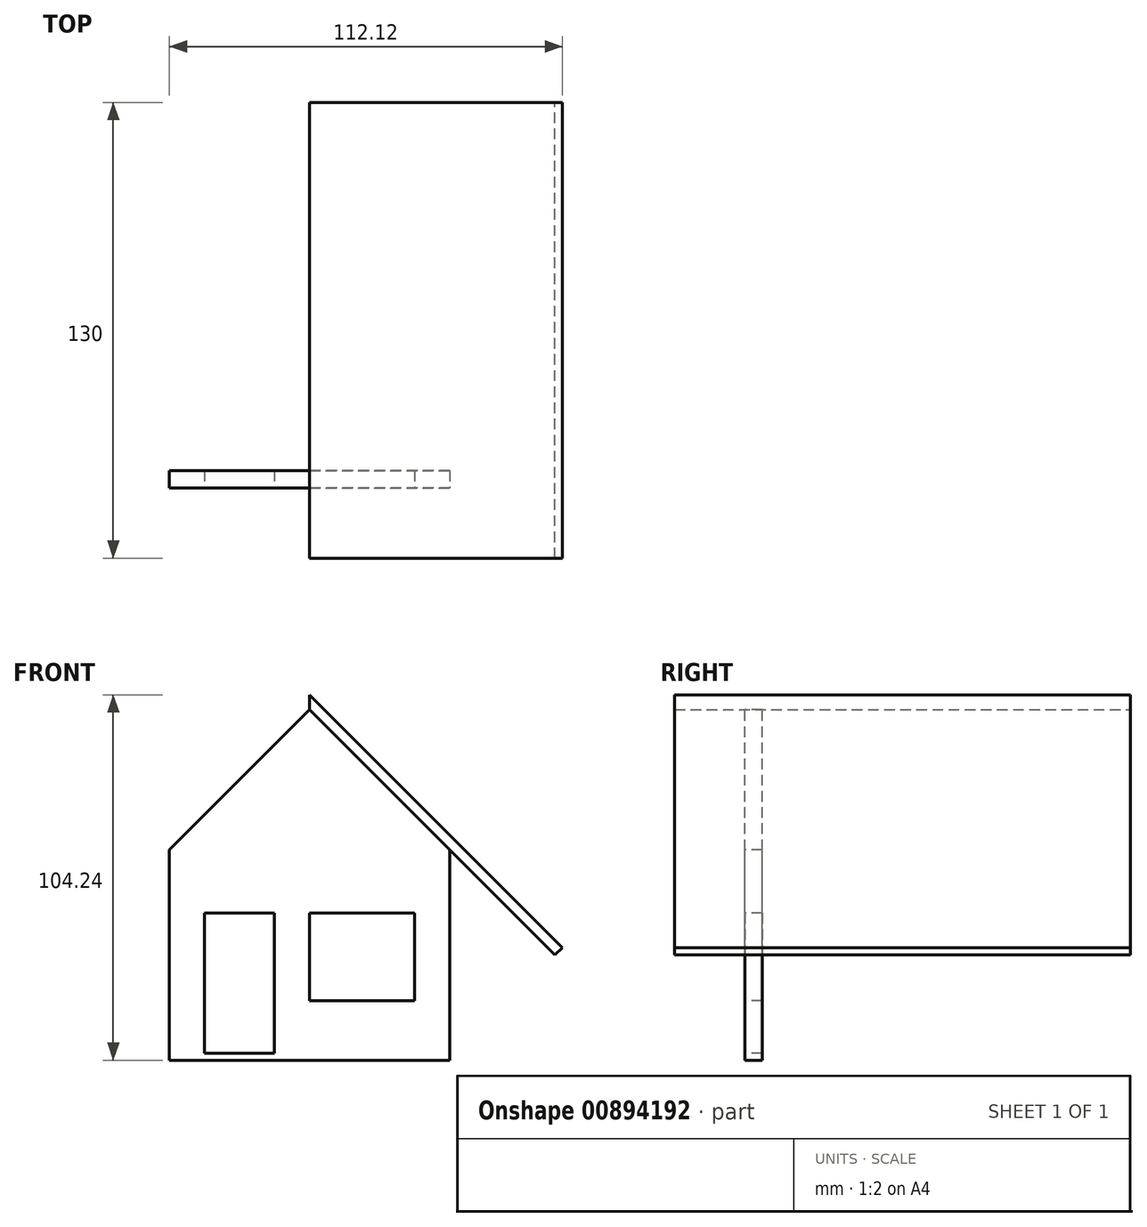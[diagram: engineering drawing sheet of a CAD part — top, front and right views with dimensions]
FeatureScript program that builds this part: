
annotation { "Feature Type Name" : "Feature", "Feature Type Description" : "" }
export const myFeature = defineFeature(function(context is Context, id is Id, definition is map)
    precondition{}
    {
        {
            var Q0;
            Q0=qCreatedBy(makeId("Top.planeOp"),FACE);
            var sketch = newSketch(context, id + "F0", { "sketchPlane" : qUnion([Q0])});
            skLineSegment(sketch, "E0.bottom", {"start": v(-80, 100) * mm, "end": v(0, 100) * mm});
            skLineSegment(sketch, "E0.top", {"start": v(-80, 0) * mm, "end": v(0, 0) * mm});
            skLineSegment(sketch, "E0.left", {"start": v(-80, 100) * mm, "end": v(-80, 0) * mm});
            skLineSegment(sketch, "E0.right", {"start": v(0, 100) * mm, "end": v(0, 0) * mm});
            skLineSegment(sketch, "E1", {"start": v(-80, 95) * mm, "end": v(0, 95) * mm});
            skLineSegment(sketch, "E2", {"start": v(-80, 5) * mm, "end": v(0, 5) * mm});
            skLineSegment(sketch, "E3", {"start": v(-7.44, 95) * mm, "end": v(-7.44, 5) * mm});
            skLineSegment(sketch, "E4", {"start": v(-69.67, 95) * mm, "end": v(-69.67, 5) * mm});
            skLineSegment(sketch, "E5", {"start": v(-69.67, 95) * mm, "end": v(-69.67, 100) * mm, "construction": true});
            skLineSegment(sketch, "E6", {"start": v(-69.67, 5) * mm, "end": v(-69.67, 0) * mm, "construction": true});
            skSolve(sketch);
        }
        {
            var Q0;
            Q0=qCreatedBy(makeId("Front.planeOp"),FACE);
            var sketch = newSketch(context, id + "F1", { "sketchPlane" : qUnion([Q0])});
            skLineSegment(sketch, "E7", {"start": v(-80, 60) * mm, "end": v(-40, 100) * mm});
            skLineSegment(sketch, "E8", {"start": v(-40, 100) * mm, "end": v(0, 60) * mm});
            skLineSegment(sketch, "E9", {"start": v(0, 0) * mm, "end": v(0, 60) * mm});
            skLineSegment(sketch, "E10", {"start": v(0, 0) * mm, "end": v(-80, 0) * mm});
            skLineSegment(sketch, "E11", {"start": v(-80, 0) * mm, "end": v(-80, 60) * mm});
            skLineSegment(sketch, "E12.bottom", {"start": v(-70, 42) * mm, "end": v(-50, 42) * mm});
            skLineSegment(sketch, "E12.top", {"start": v(-70, 2) * mm, "end": v(-50, 2) * mm});
            skLineSegment(sketch, "E12.left", {"start": v(-70, 42) * mm, "end": v(-70, 2) * mm});
            skLineSegment(sketch, "E12.right", {"start": v(-50, 42) * mm, "end": v(-50, 2) * mm});
            skLineSegment(sketch, "E13.bottom", {"start": v(-40, 42) * mm, "end": v(-10, 42) * mm});
            skLineSegment(sketch, "E13.top", {"start": v(-40, 17) * mm, "end": v(-10, 17) * mm});
            skLineSegment(sketch, "E13.left", {"start": v(-40, 42) * mm, "end": v(-40, 17) * mm});
            skLineSegment(sketch, "E13.right", {"start": v(-10, 42) * mm, "end": v(-10, 17) * mm});
            skLineSegment(sketch, "E14", {"start": v(-40, 100) * mm, "end": v(-40, 104.24) * mm});
            skLineSegment(sketch, "E15", {"start": v(-40, 104.24) * mm, "end": v(32.12, 32.12) * mm});
            skLineSegment(sketch, "E16", {"start": v(32.12, 32.12) * mm, "end": v(30, 30) * mm});
            skLineSegment(sketch, "E17", {"start": v(30, 30) * mm, "end": v(0, 60) * mm});
            skSolve(sketch);
        }
        {
            var Q0;
            Q0=makeQuery(id+"F1.imprint","IMPRINT",FACE,{"disambiguationData":[TD([[makeQuery(id+"F1.imprint","IMPRINT",EDGE,{"derivedFrom":sQuery(id+"F1.wireOp",EDGE,"E7")}),-1.0]])]});
            var Q1;
            Q1=sQuery(id+"F0.wireOp",VERTEX,"E2.start");
            extrude(context, id + "F2", {"entities" : qUnion([Q0]), "endBound" : BoundingType.UP_TO_VERTEX, "oppositeDirection" : true, "depth" : 25 * mm, "endBoundEntityVertex" : qUnion([Q1]), "offsetDistance" : 25 * mm});
        }
        {
            var Q0;
            Q0=qCreatedBy(makeId("Right.planeOp"),FACE);
            var sketch = newSketch(context, id + "F3", { "sketchPlane" : qUnion([Q0])});
            skLineSegment(sketch, "E18.bottom", {"start": v(-20, 104.24) * mm, "end": v(110, 104.24) * mm});
            skLineSegment(sketch, "E18.top", {"start": v(-20, 32.12) * mm, "end": v(110, 32.12) * mm});
            skLineSegment(sketch, "E18.left", {"start": v(-20, 104.24) * mm, "end": v(-20, 32.12) * mm});
            skLineSegment(sketch, "E18.right", {"start": v(110, 104.24) * mm, "end": v(110, 32.12) * mm});
            skSolve(sketch);
        }
        {
            var Q0;
            Q0=makeQuery(id+"F1.imprint","IMPRINT",FACE,{"disambiguationData":[TD([[makeQuery(id+"F1.imprint","IMPRINT",EDGE,{"derivedFrom":sQuery(id+"F1.wireOp",EDGE,"E8")}),1.0]])]});
            var Q1;
            Q1=sQuery(id+"F3.wireOp",VERTEX,"E18.top.start");
            var Q2;
            Q2=sQuery(id+"F3.wireOp",VERTEX,"E18.bottom.end");
            extrude(context, id + "F4", {"entities" : qUnion([Q0]), "endBound" : BoundingType.UP_TO_VERTEX, "depth" : 25 * mm, "endBoundEntityVertex" : qUnion([Q1]), "offsetDistance" : 25 * mm, "hasSecondDirection" : true, "secondDirectionBound" : SecondDirectionBoundingType.UP_TO_VERTEX, "secondDirectionOppositeDirection" : true, "secondDirectionDepth" : 25 * mm, "secondDirectionBoundEntityVertex" : qUnion([Q2])});
        }
    });
